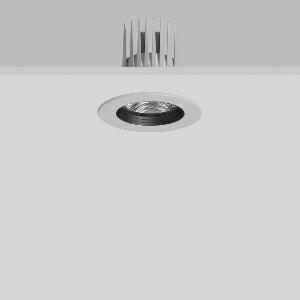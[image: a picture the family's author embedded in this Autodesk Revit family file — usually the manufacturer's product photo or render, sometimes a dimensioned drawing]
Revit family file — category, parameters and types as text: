
# Revit family: heledon_mini_e_901749_004_3_76_771f
name_source: partatom
category: Lighting Fixtures
units: mm (PartAtom-declared; Revit-internal decimal feet)

## family parameters
Cut with Voids When Loaded = No
Host = Face
Light Source = No
Part Type = Normal
Room Calculation Point = No
Round Connector Dimension = Use Diameter
Shared = No

## types (1)
- HELEDON mini E (1 x LED Modul 935, 3600 lm, 3500)
    Apparent Load = 29 VA
    Approval mark = CE
    CIE Flux Codes = 99 100 100 100 100
    Color Rendering = 92
    Color Temperature = 3500
    Default Elevation = 1800 mm
    Description = Series: HELEDON mini
Round recessed downlight. Housing: die-cast aluminium, powder-coated. Black plastic ring and recessed LED to prevent glare from the side. Optical assembly with reflector made of MIRO-Silver with 98% total light reflection for outstanding efficiency - can be changed without tools. Best colour rendering index Ra>90. Suitable for Recessed ceiling mounting. Installation without tools thanks to spring fastening system. Including separate LED converter with connecting cable 600 mm.High quality converter without flickering and stroboscopic effect. Through-wiring box (5 pole) available as accessory. The following accessories can be mounted without use of tools: interchangeable lenses, decorative glasses, honeycomb louvre, clear and frosted diffusers, white interchangeable plastic ring. 
Colour: silver
Diameter: 124 mm
Height: 3 mm
Cut-out diameter: 114 mm
Recess height: 170 mm
Luminaire: recess height: 120 mm
Lamp: LED
Socket: without socket
Colour temperature: 3500K
Colour rendering index (CRI): 92
System power: 29 W
Rated luminous flux: 3600 lm
Luminous efficiency: 124 lm/W
Control gear: Converter, dimmable, DALI
Protection class: II
Type of protection: IP 20
    Height = 0 mm  [stored 0 ft]
    Lamp = 1 x LED Modul 935
    Lamp Light Flux = 3600 lm
    Lamp count = 1
    Length = 124 mm  [stored 0.406824 ft]
    Lifetime = 50000 h
    Luminous efficacy = 124 lm/W
    Manufacturer = RZB
    ModVariant = No
    Model = 901749.004.3.76
    Mounting Place = Ceiling
    Mounting Type = Recessed
    Number of Poles = 1
    OnlyDefault = Yes
    Power Factor = 1
    Product Name = HELEDON mini E
    Product group = Recessed downlights
    ProductGroupID = 402
    Protection Class = Protection class II
    Protection Degree = IP 20
    RLX_Detail_Level = 1
    RLX_Emergency_Light_Flux = 0 lm
    RLX_Emergency_Type = 0
    RLX_Emergency_Type_DB = No
    RlxData = <blob elided: 126561 chars, md5=f5ac8e72>
    Socket = socket
    Standby Power = 0 W
    System Light Flux = 3600 lm
    System Power = 29 W
    Type Comments = Product without accessories
    Type Image = 901657.004.jpg
    URL = http://relux.com
    VarID = ---
    Voltage = 230 V
    Voltage Range = 220-240 V
    Weight = 0.00 kg
    Width = 0 mm  [stored 0 ft]

note: [stored X ft] marks values corroborated as IEEE doubles in the binary element streams (Revit-internal decimal feet)

## geometry (parser evidence)
native form markers: Blend x4, Sweep x12
no freeform markers — native parametric forms only
